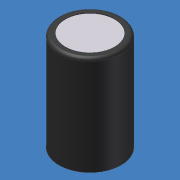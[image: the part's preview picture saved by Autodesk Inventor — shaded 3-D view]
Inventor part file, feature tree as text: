
AUTODESK INVENTOR PART (.ipt)
format: ipt  version: 2011 SP1 (Build 150282100, 282)  size: 91,136 bytes
history: native  units: mm (DEFAULTED — no unit token found)
features: extrude x2, sketch x2, fillet x1
ambient origin geometry x8: Origin, YZ Plane, XZ Plane, XY Plane, X Axis, Y Axis, Z Axis, Center Point
bodies: Solid1 (feature_tree)
feature tree (5):
  extrude  "Extrusion1"  Depth=20.32mm TaperAngle=0.0deg
  fillet  "Fillet1"  Radius=0.635mm
  extrude  "Extrusion2"  [1 undecoded]
  sketch  "Sketch1"  dims[d0=12.7mm d1=20.32mm d2=0.0mm d3=0.635mm]
  sketch  "Sketch2"  dims[d4=0.127mm d5=0.0mm]
note: 1 required parameter value undecoded (feature->parameter linkage not recoverable at this tier; creation-order binding heuristic only, values carry confidence <= 0.55)
